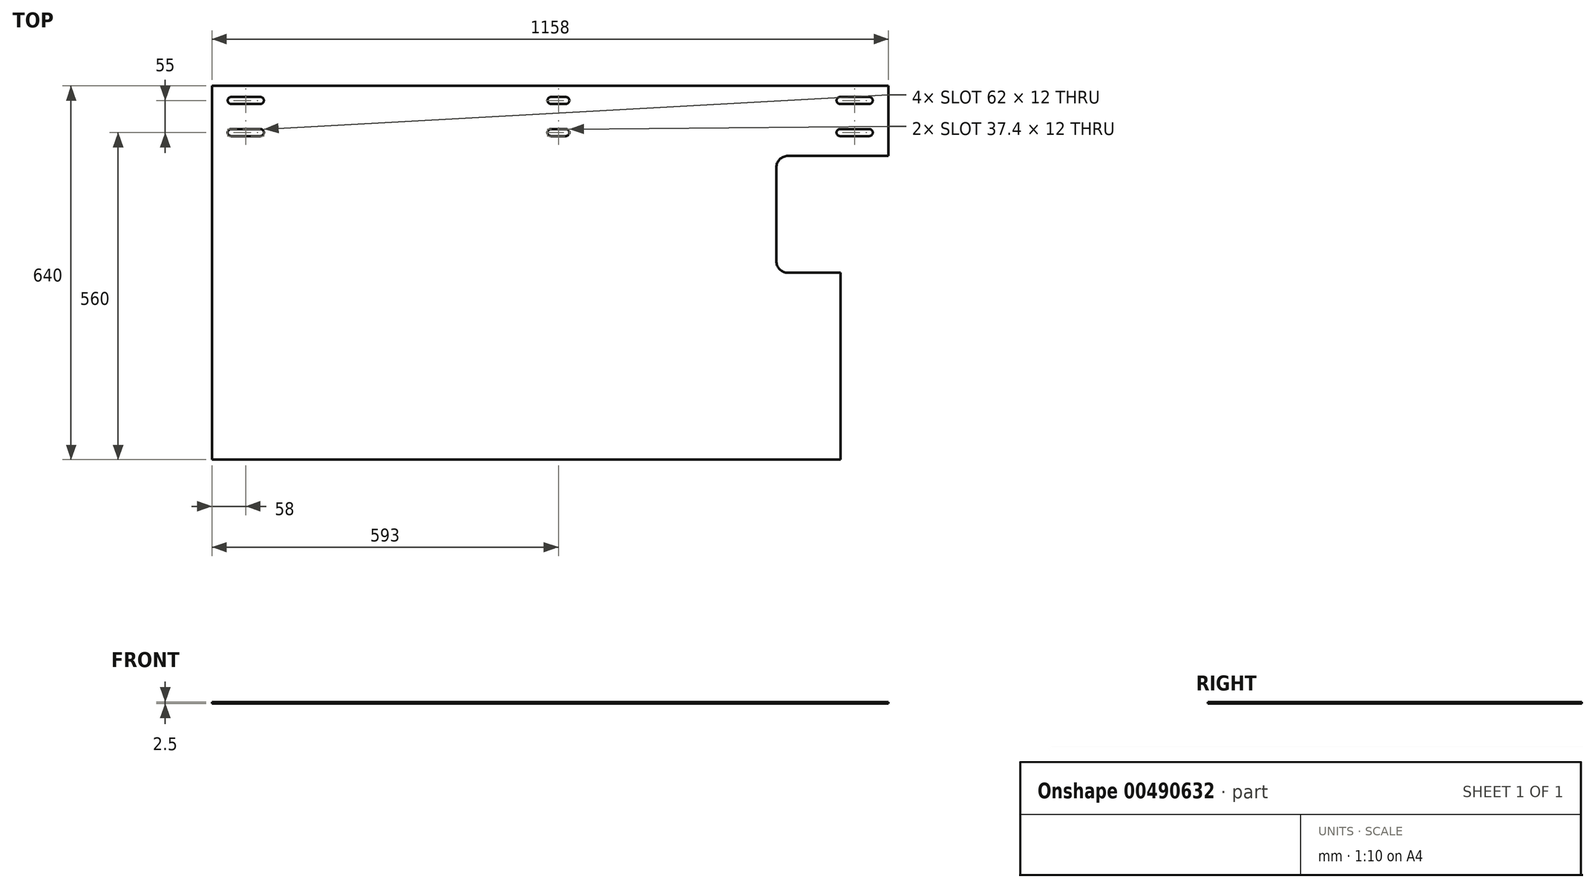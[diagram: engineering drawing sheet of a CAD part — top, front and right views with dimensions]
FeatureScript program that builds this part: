
annotation { "Feature Type Name" : "Feature", "Feature Type Description" : "" }
export const myFeature = defineFeature(function(context is Context, id is Id, definition is map)
    precondition{}
    {
        {
            var Q0;
            Q0=qCreatedBy(makeId("Top.planeOp"),FACE);
            var sketch = newSketch(context, id + "F0", { "sketchPlane" : qUnion([Q0])});
            skLineSegment(sketch, "E0", {"start": v(0, 0) * mm, "end": v(1076, 0) * mm});
            skLineSegment(sketch, "E1", {"start": v(1076, 0) * mm, "end": v(1076, 320) * mm});
            skLineSegment(sketch, "E2", {"start": v(1076, 320) * mm, "end": v(986, 320) * mm});
            skLineSegment(sketch, "E3", {"start": v(966, 340) * mm, "end": v(966, 500) * mm});
            skLineSegment(sketch, "E4", {"start": v(986, 520) * mm, "end": v(1158, 520) * mm});
            skLineSegment(sketch, "E5", {"start": v(1158, 520) * mm, "end": v(1158, 640) * mm});
            skLineSegment(sketch, "E6", {"start": v(1158, 640) * mm, "end": v(0, 640) * mm});
            skLineSegment(sketch, "E7", {"start": v(0, 640) * mm, "end": v(0, 0) * mm});
            skPoint(sketch, "E8.visualSharp", {"position": v(966, 520) * mm});
            skArc(sketch, "E8.filletArc", {"start": v(986, 520) * mm, "mid": v(971.86, 514.14) * mm, "end": v(966, 500) * mm});
            skPoint(sketch, "E9.visualSharp", {"position": v(966, 320) * mm});
            skArc(sketch, "E9.filletArc", {"start": v(966, 340) * mm, "mid": v(971.86, 325.86) * mm, "end": v(986, 320) * mm});
            skLineSegment(sketch, "E10", {"start": v(33, 621) * mm, "end": v(83, 621) * mm});
            skLineSegment(sketch, "E11", {"start": v(33, 609) * mm, "end": v(83, 609) * mm});
            skArc(sketch, "E12", {"start": v(33, 621) * mm, "mid": v(27, 615) * mm, "end": v(33, 609) * mm});
            skArc(sketch, "E13", {"start": v(83, 621) * mm, "mid": v(89, 615) * mm, "end": v(83, 609) * mm});
            skLineSegment(sketch, "E14", {"start": v(58, 621) * mm, "end": v(58, 609) * mm, "construction": true});
            skLineSegment(sketch, "E15.0.1.0", {"start": v(33, 566) * mm, "end": v(83, 566) * mm});
            skArc(sketch, "E15.0.1.1", {"start": v(33, 566) * mm, "mid": v(27, 560) * mm, "end": v(33, 554) * mm});
            skLineSegment(sketch, "E15.0.1.2", {"start": v(33, 554) * mm, "end": v(83, 554) * mm});
            skArc(sketch, "E15.0.1.3", {"start": v(83, 566) * mm, "mid": v(89, 560) * mm, "end": v(83, 554) * mm});
            skLineSegment(sketch, "E15.1.0.0", {"start": v(1075, 621) * mm, "end": v(1125, 621) * mm});
            skArc(sketch, "E15.1.0.1", {"start": v(1075, 621) * mm, "mid": v(1069, 615) * mm, "end": v(1075, 609) * mm});
            skLineSegment(sketch, "E15.1.0.2", {"start": v(1075, 609) * mm, "end": v(1125, 609) * mm});
            skArc(sketch, "E15.1.0.3", {"start": v(1125, 621) * mm, "mid": v(1131, 615) * mm, "end": v(1125, 609) * mm});
            skLineSegment(sketch, "E15.1.1.0", {"start": v(1075, 566) * mm, "end": v(1125, 566) * mm});
            skArc(sketch, "E15.1.1.1", {"start": v(1075, 566) * mm, "mid": v(1069, 560) * mm, "end": v(1075, 554) * mm});
            skLineSegment(sketch, "E15.1.1.2", {"start": v(1075, 554) * mm, "end": v(1125, 554) * mm});
            skArc(sketch, "E15.1.1.3", {"start": v(1125, 566) * mm, "mid": v(1131, 560) * mm, "end": v(1125, 554) * mm});
            skLineSegment(sketch, "E15.direction2", {"start": v(33, 609) * mm, "end": v(33, 554) * mm, "construction": true});
            skLineSegment(sketch, "E16", {"start": v(1100, 621) * mm, "end": v(1100, 609) * mm, "construction": true});
            skLineSegment(sketch, "E17", {"start": v(580.3, 609) * mm, "end": v(605.7, 609) * mm});
            skLineSegment(sketch, "E18", {"start": v(580.3, 621) * mm, "end": v(605.7, 621) * mm});
            skArc(sketch, "E19", {"start": v(580.3, 609) * mm, "mid": v(574.3, 615) * mm, "end": v(580.3, 621) * mm});
            skArc(sketch, "E20", {"start": v(605.7, 621) * mm, "mid": v(611.7, 615) * mm, "end": v(605.7, 609) * mm});
            skLineSegment(sketch, "E21", {"start": v(593, 621) * mm, "end": v(593, 609) * mm, "construction": true});
            skArc(sketch, "E22.0.1.0", {"start": v(580.3, 554) * mm, "mid": v(574.3, 560) * mm, "end": v(580.3, 566) * mm});
            skLineSegment(sketch, "E22.0.1.1", {"start": v(580.3, 566) * mm, "end": v(605.7, 566) * mm});
            skLineSegment(sketch, "E22.0.1.2", {"start": v(580.3, 554) * mm, "end": v(605.7, 554) * mm});
            skArc(sketch, "E22.0.1.3", {"start": v(605.7, 566) * mm, "mid": v(611.7, 560) * mm, "end": v(605.7, 554) * mm});
            skLineSegment(sketch, "E22.direction1", {"start": v(580.3, 609) * mm, "end": v(605.3, 609) * mm, "construction": true});
            skLineSegment(sketch, "E22.direction2", {"start": v(580.3, 609) * mm, "end": v(580.3, 554) * mm, "construction": true});
            skSolve(sketch);
        }
        {
            var Q0;
            Q0=makeQuery(id+"F0.imprint","IMPRINT",FACE,{"disambiguationData":[TD([[makeQuery(id+"F0.imprint","IMPRINT",EDGE,{"derivedFrom":sQuery(id+"F0.wireOp",EDGE,"E0")}),1.0]])]});
            extrude(context, id + "F1", {"entities" : qUnion([Q0]), "depth" : 2.5 * mm});
        }
    });
